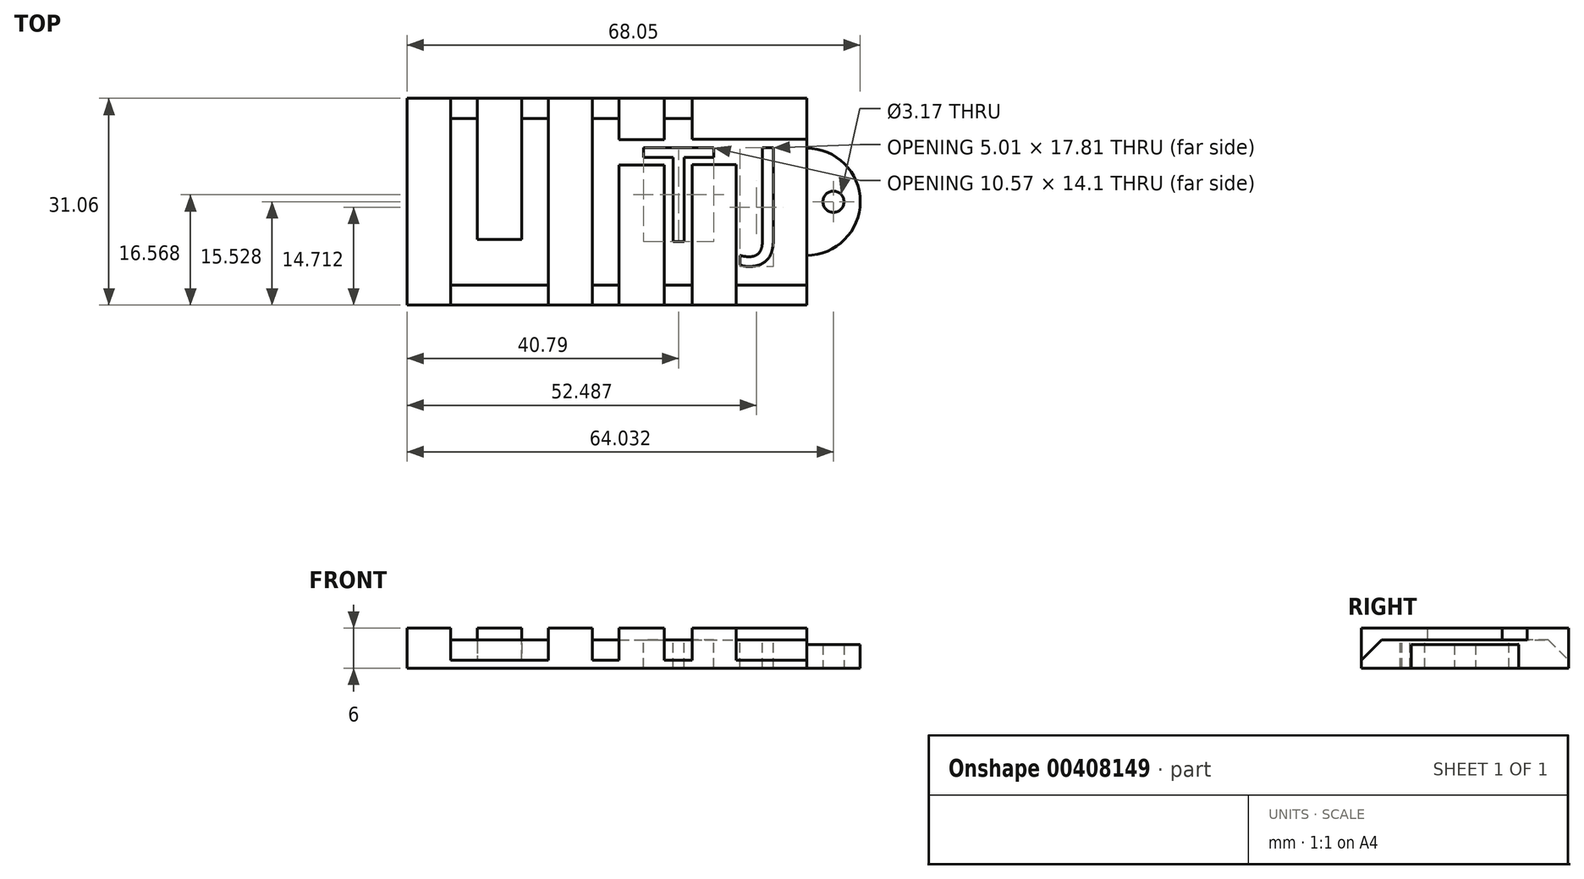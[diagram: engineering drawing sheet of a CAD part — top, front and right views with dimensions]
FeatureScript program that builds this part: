
annotation { "Feature Type Name" : "Feature", "Feature Type Description" : "" }
export const myFeature = defineFeature(function(context is Context, id is Id, definition is map)
    precondition{}
    {
        {
            var Q0;
            Q0=qCreatedBy(makeId("Top.planeOp"),FACE);
            var sketch = newSketch(context, id + "F0", { "sketchPlane" : qUnion([Q0])});
            skLineSegment(sketch, "E0.bottom", {"start": v(-74.33, -7.04) * mm, "end": v(-67.75, -7.04) * mm});
            skLineSegment(sketch, "E0.top", {"start": v(-74.33, -38.1) * mm, "end": v(-67.75, -38.1) * mm});
            skLineSegment(sketch, "E0.left", {"start": v(-74.33, -7.04) * mm, "end": v(-74.33, -38.1) * mm});
            skLineSegment(sketch, "E0.right", {"start": v(-14.33, -7.04) * mm, "end": v(-14.33, -13.21) * mm});
            skLineSegment(sketch, "E1", {"start": v(-67.75, -7.04) * mm, "end": v(-67.75, -38.1) * mm});
            skLineSegment(sketch, "E2", {"start": v(-63.76, -7.04) * mm, "end": v(-63.76, -28.21) * mm});
            skLineSegment(sketch, "E3", {"start": v(-63.76, -28.21) * mm, "end": v(-57.1, -28.21) * mm});
            skLineSegment(sketch, "E4", {"start": v(-57.1, -28.21) * mm, "end": v(-57.1, -7.04) * mm});
            skLineSegment(sketch, "E5", {"start": v(-53.1, -7.04) * mm, "end": v(-53.1, -38.1) * mm});
            skLineSegment(sketch, "E6", {"start": v(-46.52, -38.1) * mm, "end": v(-46.52, -7.04) * mm});
            skLineSegment(sketch, "E7", {"start": v(-42.48, -7.04) * mm, "end": v(-42.48, -13.24) * mm});
            skLineSegment(sketch, "E8", {"start": v(-42.48, -13.24) * mm, "end": v(-35.72, -13.24) * mm});
            skLineSegment(sketch, "E9", {"start": v(-35.72, -13.24) * mm, "end": v(-35.72, -7.04) * mm});
            skLineSegment(sketch, "E10", {"start": v(-42.48, -38.1) * mm, "end": v(-42.48, -17.05) * mm});
            skLineSegment(sketch, "E11", {"start": v(-42.48, -17.05) * mm, "end": v(-35.72, -17.05) * mm});
            skLineSegment(sketch, "E12", {"start": v(-35.72, -17.05) * mm, "end": v(-35.72, -38.1) * mm});
            skLineSegment(sketch, "E13", {"start": v(-24.92, -17) * mm, "end": v(-24.92, -38.1) * mm});
            skLineSegment(sketch, "E14", {"start": v(-31.54, -7.04) * mm, "end": v(-31.54, -13.21) * mm});
            skLineSegment(sketch, "E15", {"start": v(-31.54, -13.21) * mm, "end": v(-14.33, -13.21) * mm});
            skLineSegment(sketch, "E16", {"start": v(-31.54, -38.1) * mm, "end": v(-31.54, -17) * mm});
            skPoint(sketch, "E16.startSnap0", {"position": v(-31.54, -10.13) * mm});
            skLineSegment(sketch, "E17", {"start": v(-31.54, -17) * mm, "end": v(-24.92, -17) * mm});
            skCircle(sketch, "E18", {"center": v(-10.3, -22.57) * mm, "radius": 1.59 * mm});
            skArc(sketch, "E19", {"start": v(-14.33, -30.62) * mm, "mid": v(-6.29, -22.57) * mm, "end": v(-14.33, -14.52) * mm});
            skLineSegment(sketch, "E20.trimOffspring", {"start": v(-63.76, -7.04) * mm, "end": v(-57.1, -7.04) * mm});
            skLineSegment(sketch, "E21.trimOffspring", {"start": v(-53.1, -7.04) * mm, "end": v(-46.52, -7.04) * mm});
            skLineSegment(sketch, "E22.trimOffspring", {"start": v(-42.48, -7.04) * mm, "end": v(-35.72, -7.04) * mm});
            skLineSegment(sketch, "E23.trimOffspring", {"start": v(-31.54, -7.04) * mm, "end": v(-14.33, -7.04) * mm});
            skLineSegment(sketch, "E24.trimOffspring", {"start": v(-31.54, -38.1) * mm, "end": v(-24.92, -38.1) * mm});
            skLineSegment(sketch, "E25.trimOffspring", {"start": v(-42.48, -38.1) * mm, "end": v(-35.72, -38.1) * mm});
            skLineSegment(sketch, "E26.trimOffspring", {"start": v(-53.1, -38.1) * mm, "end": v(-46.52, -38.1) * mm});
            skLineSegment(sketch, "E27.trimOffspring", {"start": v(-14.33, -14.52) * mm, "end": v(-14.33, -30.62) * mm});
            skPoint(sketch, "E28.orphan", {"position": v(-14.33, -38.1) * mm});
            skLineSegment(sketch, "E29", {"start": v(-74.33, -7.04) * mm, "end": v(-14.33, -7.04) * mm});
            skLineSegment(sketch, "E30", {"start": v(-74.33, -38.1) * mm, "end": v(-14.33, -38.1) * mm});
            skLineSegment(sketch, "E31", {"start": v(-14.33, -13.21) * mm, "end": v(-14.33, -38.1) * mm});
            skSolve(sketch);
        }
        {
            var Q0;
            {var subQ2=sQuery(id+"F0.wireOp",EDGE,"E1");Q0=makeQuery(id+"F0.imprint","IMPRINT",FACE,{"disambiguationData":[TD([[makeQuery(id+"F0.imprint","IMPRINT",EDGE,{"derivedFrom":subQ2}),1.0]])]});}
            var Q1;
            {var subQ12=sQuery(id+"F0.wireOp",EDGE,"E6");Q1=makeQuery(id+"F0.imprint","IMPRINT",FACE,{"disambiguationData":[TD([[makeQuery(id+"F0.imprint","IMPRINT",EDGE,{"derivedFrom":subQ12}),-1.0]])]});}
            extrude(context, id + "F1", {"entities" : qUnion([Q0, Q1]), "depth" : 4.2 * mm});
        }
        {
            var Q0;
            {var subQ0=sQuery(id+"F0.wireOp",EDGE,"E0.left");Q0=makeQuery(id+"F0.imprint","IMPRINT",FACE,{"disambiguationData":[TD([[makeQuery(id+"F0.imprint","IMPRINT",EDGE,{"derivedFrom":subQ0}),1.0]])]});}
            var Q1;
            {var subQ0=sQuery(id+"F0.wireOp",EDGE,"E2");Q1=makeQuery(id+"F0.imprint","IMPRINT",FACE,{"disambiguationData":[TD([[makeQuery(id+"F0.imprint","IMPRINT",EDGE,{"derivedFrom":subQ0}),1.0]])]});}
            var Q2;
            {var subQ0=sQuery(id+"F0.wireOp",EDGE,"E5");Q2=makeQuery(id+"F0.imprint","IMPRINT",FACE,{"disambiguationData":[TD([[makeQuery(id+"F0.imprint","IMPRINT",EDGE,{"derivedFrom":subQ0}),1.0]])]});}
            var Q3;
            {var subQ0=sQuery(id+"F0.wireOp",EDGE,"E7");Q3=makeQuery(id+"F0.imprint","IMPRINT",FACE,{"disambiguationData":[TD([[makeQuery(id+"F0.imprint","IMPRINT",EDGE,{"derivedFrom":subQ0}),1.0]])]});}
            var Q4;
            {var subQ0=sQuery(id+"F0.wireOp",EDGE,"E10");Q4=makeQuery(id+"F0.imprint","IMPRINT",FACE,{"disambiguationData":[TD([[makeQuery(id+"F0.imprint","IMPRINT",EDGE,{"derivedFrom":subQ0}),-1.0]])]});}
            var Q5;
            {var subQ0=sQuery(id+"F0.wireOp",EDGE,"E13");Q5=makeQuery(id+"F0.imprint","IMPRINT",FACE,{"disambiguationData":[TD([[makeQuery(id+"F0.imprint","IMPRINT",EDGE,{"derivedFrom":subQ0}),-1.0]])]});}
            var Q6;
            {var subQ0=sQuery(id+"F0.wireOp",EDGE,"E0.right");Q6=makeQuery(id+"F0.imprint","IMPRINT",FACE,{"disambiguationData":[TD([[makeQuery(id+"F0.imprint","IMPRINT",EDGE,{"derivedFrom":subQ0}),-1.0]])]});}
            extrude(context, id + "F2", {"entities" : qUnion([Q0, Q1, Q2, Q3, Q4, Q5, Q6]), "operationType" : NewBodyOperationType.ADD, "depth" : 6 * mm});
        }
        {
            var Q0;
            Q0=makeQuery(id+"F0.imprint","IMPRINT",FACE,{"disambiguationData":[TD([[makeQuery(id+"F0.imprint","IMPRINT",EDGE,{"derivedFrom":sQuery(id+"F0.wireOp",EDGE,"E18")}),-1.0]])]});
            extrude(context, id + "F3", {"entities" : qUnion([Q0]), "operationType" : NewBodyOperationType.ADD, "depth" : 3.5 * mm});
        }
        {
            var Q0;
            Q0=makeQuery(id+"F1.opExtrude","CAP_FACE",FACE,{"disambiguationData":[OSD([sQuery(id+"F0.wireOp",EDGE,"E6"),sQuery(id+"F0.wireOp",EDGE,"E7"),sQuery(id+"F0.wireOp",EDGE,"E8"),sQuery(id+"F0.wireOp",EDGE,"E9"),sQuery(id+"F0.wireOp",EDGE,"E10"),sQuery(id+"F0.wireOp",EDGE,"E11"),sQuery(id+"F0.wireOp",EDGE,"E12"),sQuery(id+"F0.wireOp",EDGE,"E13"),sQuery(id+"F0.wireOp",EDGE,"E14"),sQuery(id+"F0.wireOp",EDGE,"E15"),sQuery(id+"F0.wireOp",EDGE,"E16"),sQuery(id+"F0.wireOp",EDGE,"E17"),sQuery(id+"F0.wireOp",EDGE,"E29"),sQuery(id+"F0.wireOp",EDGE,"E30"),sQuery(id+"F0.wireOp",EDGE,"E31")])],"isStart":false});
            var sketch = newSketch(context, id + "F4", { "sketchPlane" : qUnion([Q0])});
            skPoint(sketch, "E32.endSnap0", {"position": v(-28.23, -15.1) * mm});
            skPoint(sketch, "E33.start.orphan", {"position": v(-39.1, -13.24) * mm});
            skPoint(sketch, "E34.orphan", {"position": v(-28.23, -13.21) * mm});
            skPoint(sketch, "E35.orphan", {"position": v(-28.23, -17) * mm});
            skPoint(sketch, "E36.start.orphan", {"position": v(-39.1, -17.05) * mm});
            skText(sketch, "E37", { "text": "J", "fontName": "OpenSans-Regular.ttf"});
            skText(sketch, "E38", { "text": "T", "fontName": "OpenSans-Regular.ttf"});
            const initialGuessF4  = {"E37": [-0.02281, -0.02858, 1, 0, 0.01422], "E38": [-0.039, -0.02858, 1, 0, 0.01422]};
            skSetInitialGuess(sketch, initialGuessF4);
            skSolve(sketch);
        }
        {
            var Q0;
            Q0=makeQuery(id+"F4.imprint","IMPRINT",FACE,{"disambiguationData":[TD([[makeQuery(id+"F4.imprint","IMPRINT",EDGE,{"derivedFrom":sQuery(id+"F4.wireOp",EDGE,"E38.sketch_text.stroke-0")}),-1.0]])]});
            var Q1;
            Q1=makeQuery(id+"F4.imprint","IMPRINT",FACE,{"disambiguationData":[TD([[makeQuery(id+"F4.imprint","IMPRINT",EDGE,{"derivedFrom":sQuery(id+"F4.wireOp",EDGE,"E37.sketch_text.stroke-0")}),-1.0]])]});
            extrude(context, id + "F5", {"entities" : qUnion([Q0, Q1]), "operationType" : NewBodyOperationType.REMOVE, "oppositeDirection" : true, "depth" : 25 * mm});
        }
        {
            var Q0;
            {var subQ0=sQuery(id+"F0.wireOp",EDGE,"E29");Q0=makeQuery(id+"F1.opExtrude","CAP_EDGE",EDGE,{"disambiguationData":[OSD([subQ0]),TDD([makeQuery(id+"F0.imprint","IMPRINT",EDGE,{"disambiguationData":[TD([[makeQuery(id+"F0.imprint","INTERSECT",VERTEX,{"derivedFrom":[sQuery(id+"F0.wireOp",EDGE,"E1"),subQ0]}),-1.0]])],"derivedFrom":subQ0})])],"isStart":false});}
            var Q1;
            {var subQ0=sQuery(id+"F0.wireOp",EDGE,"E29");Q1=makeQuery(id+"F1.opExtrude","CAP_EDGE",EDGE,{"disambiguationData":[OSD([subQ0]),TDD([makeQuery(id+"F0.imprint","IMPRINT",EDGE,{"disambiguationData":[TD([[makeQuery(id+"F0.imprint","INTERSECT",VERTEX,{"derivedFrom":[sQuery(id+"F0.wireOp",EDGE,"E4"),subQ0]}),-1.0]])],"derivedFrom":subQ0})])],"isStart":false});}
            var Q2;
            {var subQ0=sQuery(id+"F0.wireOp",EDGE,"E29");Q2=makeQuery(id+"F1.opExtrude","CAP_EDGE",EDGE,{"disambiguationData":[OSD([subQ0]),TDD([makeQuery(id+"F0.imprint","IMPRINT",EDGE,{"disambiguationData":[TD([[makeQuery(id+"F0.imprint","INTERSECT",VERTEX,{"derivedFrom":[sQuery(id+"F0.wireOp",EDGE,"E6"),subQ0]}),-1.0]])],"derivedFrom":subQ0})])],"isStart":false});}
            var Q3;
            {var subQ0=sQuery(id+"F0.wireOp",EDGE,"E29");Q3=makeQuery(id+"F1.opExtrude","CAP_EDGE",EDGE,{"disambiguationData":[OSD([subQ0]),TDD([makeQuery(id+"F0.imprint","IMPRINT",EDGE,{"disambiguationData":[TD([[makeQuery(id+"F0.imprint","INTERSECT",VERTEX,{"derivedFrom":[sQuery(id+"F0.wireOp",EDGE,"E9"),subQ0]}),-1.0]])],"derivedFrom":subQ0})])],"isStart":false});}
            var Q4;
            {var subQ0=sQuery(id+"F0.wireOp",EDGE,"E30");Q4=makeQuery(id+"F1.opExtrude","CAP_EDGE",EDGE,{"disambiguationData":[OSD([subQ0]),TDD([makeQuery(id+"F0.imprint","IMPRINT",EDGE,{"disambiguationData":[TD([[makeQuery(id+"F0.imprint","INTERSECT",VERTEX,{"derivedFrom":[sQuery(id+"F0.wireOp",EDGE,"E1"),subQ0]}),-1.0]])],"derivedFrom":subQ0})])],"isStart":false});}
            var Q5;
            {var subQ0=sQuery(id+"F0.wireOp",EDGE,"E30");Q5=makeQuery(id+"F1.opExtrude","CAP_EDGE",EDGE,{"disambiguationData":[OSD([subQ0]),TDD([makeQuery(id+"F0.imprint","IMPRINT",EDGE,{"disambiguationData":[TD([[makeQuery(id+"F0.imprint","INTERSECT",VERTEX,{"derivedFrom":[sQuery(id+"F0.wireOp",EDGE,"E6"),subQ0]}),-1.0]])],"derivedFrom":subQ0})])],"isStart":false});}
            var Q6;
            {var subQ0=sQuery(id+"F0.wireOp",EDGE,"E30");Q6=makeQuery(id+"F1.opExtrude","CAP_EDGE",EDGE,{"disambiguationData":[OSD([subQ0]),TDD([makeQuery(id+"F0.imprint","IMPRINT",EDGE,{"disambiguationData":[TD([[makeQuery(id+"F0.imprint","INTERSECT",VERTEX,{"derivedFrom":[sQuery(id+"F0.wireOp",EDGE,"E12"),subQ0]}),-1.0]])],"derivedFrom":subQ0})])],"isStart":false});}
            var Q7;
            {var subQ0=sQuery(id+"F0.wireOp",EDGE,"E30");Q7=makeQuery(id+"F1.opExtrude","CAP_EDGE",EDGE,{"disambiguationData":[OSD([subQ0]),TDD([makeQuery(id+"F0.imprint","IMPRINT",EDGE,{"disambiguationData":[TD([[makeQuery(id+"F0.imprint","INTERSECT",VERTEX,{"derivedFrom":[sQuery(id+"F0.wireOp",EDGE,"E13"),subQ0]}),-1.0]])],"derivedFrom":subQ0})])],"isStart":false});}
            chamfer(context, id + "F6", {"entities" : qUnion([Q0, Q1, Q2, Q3, Q4, Q5, Q6, Q7]), "width" : 3 * mm, "tangentPropagation" : true});
        }
        {
            var Q0;
            {var subQ0=sQuery(id+"F0.wireOp",EDGE,"E31");var subQ1=sQuery(id+"F0.wireOp",EDGE,"E30");var subQ2=sQuery(id+"F0.wireOp",EDGE,"E17");var subQ3=sQuery(id+"F0.wireOp",EDGE,"E16");var subQ4=sQuery(id+"F0.wireOp",EDGE,"E13");var subQ5=sQuery(id+"F0.wireOp",EDGE,"E12");var subQ6=sQuery(id+"F0.wireOp",EDGE,"E11");var subQ7=sQuery(id+"F0.wireOp",EDGE,"E10");var subQ8=sQuery(id+"F0.wireOp",EDGE,"E29");var subQ9=sQuery(id+"F0.wireOp",EDGE,"E9");var subQ10=sQuery(id+"F0.wireOp",EDGE,"E8");var subQ11=sQuery(id+"F0.wireOp",EDGE,"E7");var subQ12=sQuery(id+"F0.wireOp",EDGE,"E6");var subQ13=sQuery(id+"F0.wireOp",EDGE,"E5");var subQ14=sQuery(id+"F0.wireOp",EDGE,"E4");var subQ15=sQuery(id+"F0.wireOp",EDGE,"E3");var subQ16=sQuery(id+"F0.wireOp",EDGE,"E2");var subQ17=sQuery(id+"F0.wireOp",EDGE,"E15");var subQ18=sQuery(id+"F0.wireOp",EDGE,"E14");var subQ19=sQuery(id+"F0.wireOp",EDGE,"E1");Q0=makeQuery(id+"F3.boolean.opBoolean","MERGE",FACE,{"derivedFrom":[makeQuery(id+"F2.boolean.opBoolean","MERGE",FACE,{"derivedFrom":[makeQuery(id+"F1.opExtrude","CAP_FACE",FACE,{"disambiguationData":[OSD([subQ19,subQ16,subQ15,subQ14,subQ13,subQ8,subQ1])],"isStart":true}),makeQuery(id+"F1.opExtrude","CAP_FACE",FACE,{"disambiguationData":[OSD([subQ12,subQ11,subQ10,subQ9,subQ7,subQ6,subQ5,subQ4,subQ18,subQ17,subQ3,subQ2,subQ8,subQ1,subQ0])],"isStart":true}),makeQuery(id+"F2.opExtrude","CAP_FACE",FACE,{"disambiguationData":[OSD([sQuery(id+"F0.wireOp",EDGE,"E0.left"),subQ19,subQ8,subQ1])],"isStart":true}),makeQuery(id+"F2.opExtrude","CAP_FACE",FACE,{"disambiguationData":[OSD([sQuery(id+"F0.wireOp",EDGE,"E0.right"),subQ18,subQ17,subQ8])],"isStart":true}),makeQuery(id+"F2.opExtrude","CAP_FACE",FACE,{"disambiguationData":[OSD([subQ16,subQ15,subQ14,subQ8])],"isStart":true}),makeQuery(id+"F2.opExtrude","CAP_FACE",FACE,{"disambiguationData":[OSD([subQ13,subQ12,subQ8,subQ1])],"isStart":true}),makeQuery(id+"F2.opExtrude","CAP_FACE",FACE,{"disambiguationData":[OSD([subQ11,subQ10,subQ9,subQ8])],"isStart":true}),makeQuery(id+"F2.opExtrude","CAP_FACE",FACE,{"disambiguationData":[OSD([subQ7,subQ6,subQ5,subQ1])],"isStart":true}),makeQuery(id+"F2.opExtrude","CAP_FACE",FACE,{"disambiguationData":[OSD([subQ4,subQ3,subQ2,subQ1])],"isStart":true})]}),makeQuery(id+"F3.opExtrude","CAP_FACE",FACE,{"disambiguationData":[OSD([sQuery(id+"F0.wireOp",EDGE,"E18"),sQuery(id+"F0.wireOp",EDGE,"E19"),subQ0])],"isStart":true})]});}
            var sketch = newSketch(context, id + "F7", { "sketchPlane" : qUnion([Q0])});
            skLineSegment(sketch, "E39", {"start": v(0, 0) * mm, "end": v(-44.33, 22.96) * mm});
            skPoint(sketch, "E39.endSnap0", {"position": v(-44.33, 7.04) * mm});
            skSolve(sketch);
        }
        {
            var Q0;
            Q0=makeQuery(id+"F1.opExtrude","SWEPT_BODY",BODY,{"disambiguationData":[OSD([sQuery(id+"F0.wireOp",EDGE,"E1"),sQuery(id+"F0.wireOp",EDGE,"E2"),sQuery(id+"F0.wireOp",EDGE,"E3"),sQuery(id+"F0.wireOp",EDGE,"E4"),sQuery(id+"F0.wireOp",EDGE,"E5"),sQuery(id+"F0.wireOp",EDGE,"E29"),sQuery(id+"F0.wireOp",EDGE,"E30")])]});
            var Q1;
            Q1=sQuery(id+"F7.wireOp",EDGE,"E39");
            transform(context, id + "F8", {"entities" : qUnion([Q0]), "transformType" : TransformType.TRANSLATION_ENTITY, "oppositeDirectionEntity" : true, "transformLine" : qUnion([Q1]), "makeCopy" : false});
        }
    });
